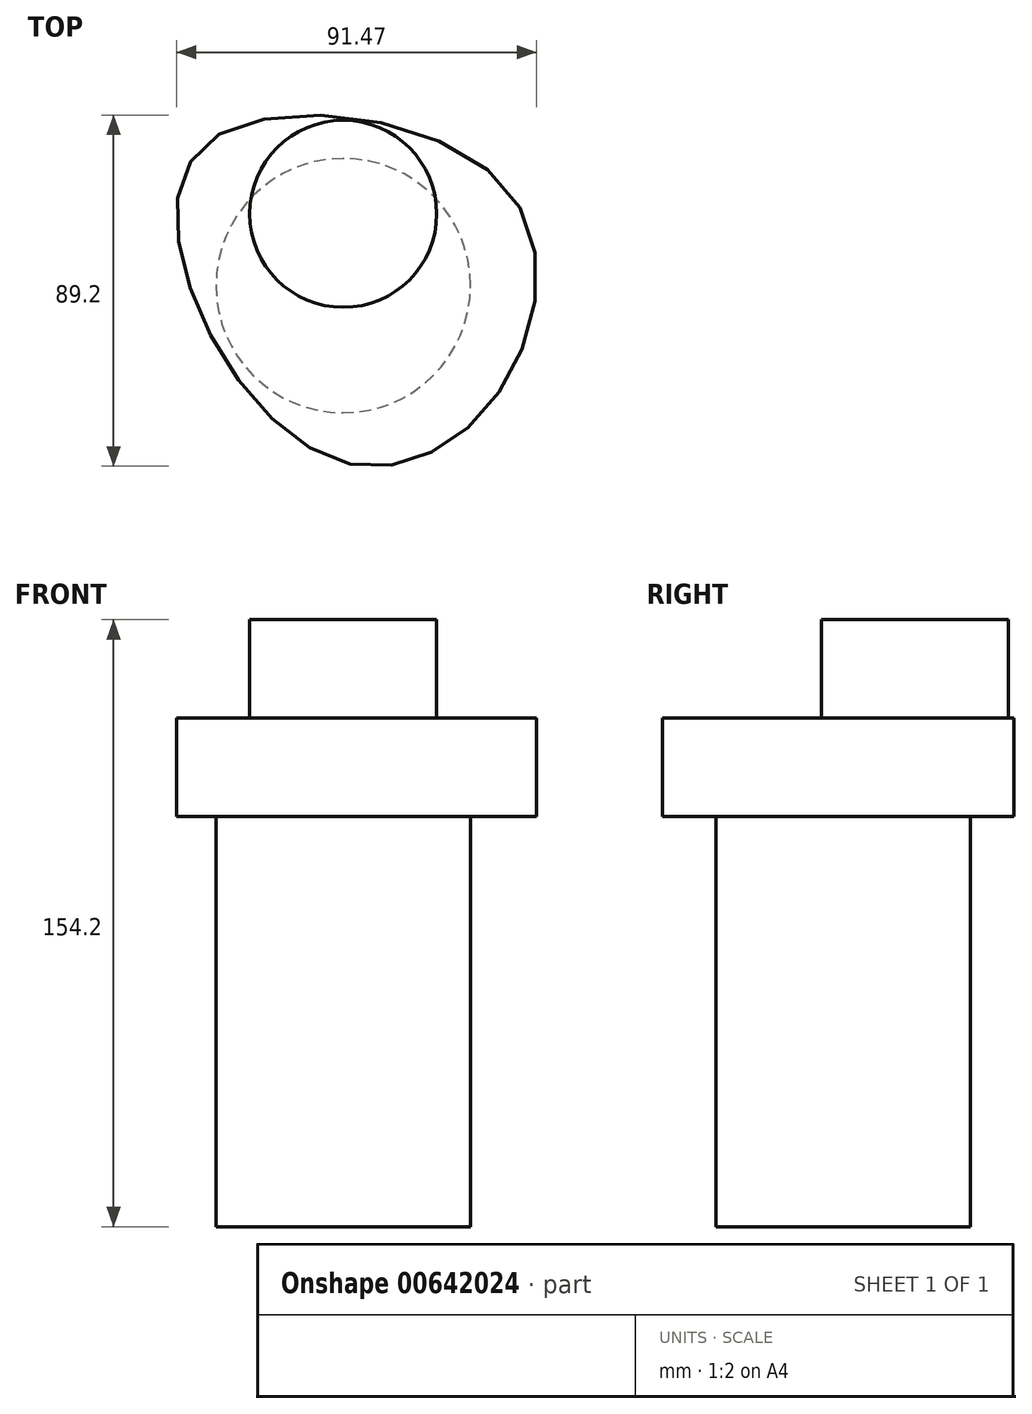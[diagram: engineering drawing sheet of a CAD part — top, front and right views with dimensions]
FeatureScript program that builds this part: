
annotation { "Feature Type Name" : "Feature", "Feature Type Description" : "" }
export const myFeature = defineFeature(function(context is Context, id is Id, definition is map)
    precondition{}
    {
        {
            var Q0;
            Q0=qCreatedBy(makeId("Top.planeOp"),FACE);
            var sketch = newSketch(context, id + "F0", { "sketchPlane" : qUnion([Q0])});
            skFitSpline(sketch, "E0", {"points": [v(-31.53, 38.42) * mm, v(40.54, 25.8) * mm, v(39.46, -27.2) * mm, v(0, -44.87) * mm, v(-39.1, 0) * mm, v(-31.53, 38.42) * mm]});
            skSolve(sketch);
        }
        {
            var Q0;
            Q0 = qSketchRegion(id + "F0", true);
            extrude(context, id + "F1", {"entities" : qUnion([Q0]), "depth" : 25 * mm, "offsetDistance" : 25 * mm});
        }
        {
            var Q0;
            Q0=makeQuery(id+"F1.opExtrude","CAP_FACE",FACE,{"disambiguationData":[OSD([sQuery(id+"F0.wireOp",EDGE,"E0")])],"isStart":false});
            var sketch = newSketch(context, id + "F2", { "sketchPlane" : qUnion([Q0])});
            skCircle(sketch, "E1", {"center": v(0, 18.23) * mm, "radius": 23.74 * mm});
            skSolve(sketch);
        }
        {
            var Q0;
            Q0 = qSketchRegion(id + "F2", true);
            extrude(context, id + "F3", {"entities" : qUnion([Q0]), "depth" : 25 * mm, "offsetDistance" : 25 * mm});
        }
        {
            var Q0;
            Q0=qCreatedBy(makeId("Top.planeOp"),FACE);
            var sketch = newSketch(context, id + "F4", { "sketchPlane" : qUnion([Q0])});
            skCircle(sketch, "E2", {"center": v(0, 0) * mm, "radius": 32.32 * mm});
            skSolve(sketch);
        }
        {
            var Q0;
            Q0 = qSketchRegion(id + "F4", true);
            extrude(context, id + "F5", {"entities" : qUnion([Q0]), "operationType" : NewBodyOperationType.ADD, "oppositeDirection" : true, "depth" : 104.2 * mm, "offsetDistance" : 25 * mm});
        }
    });
